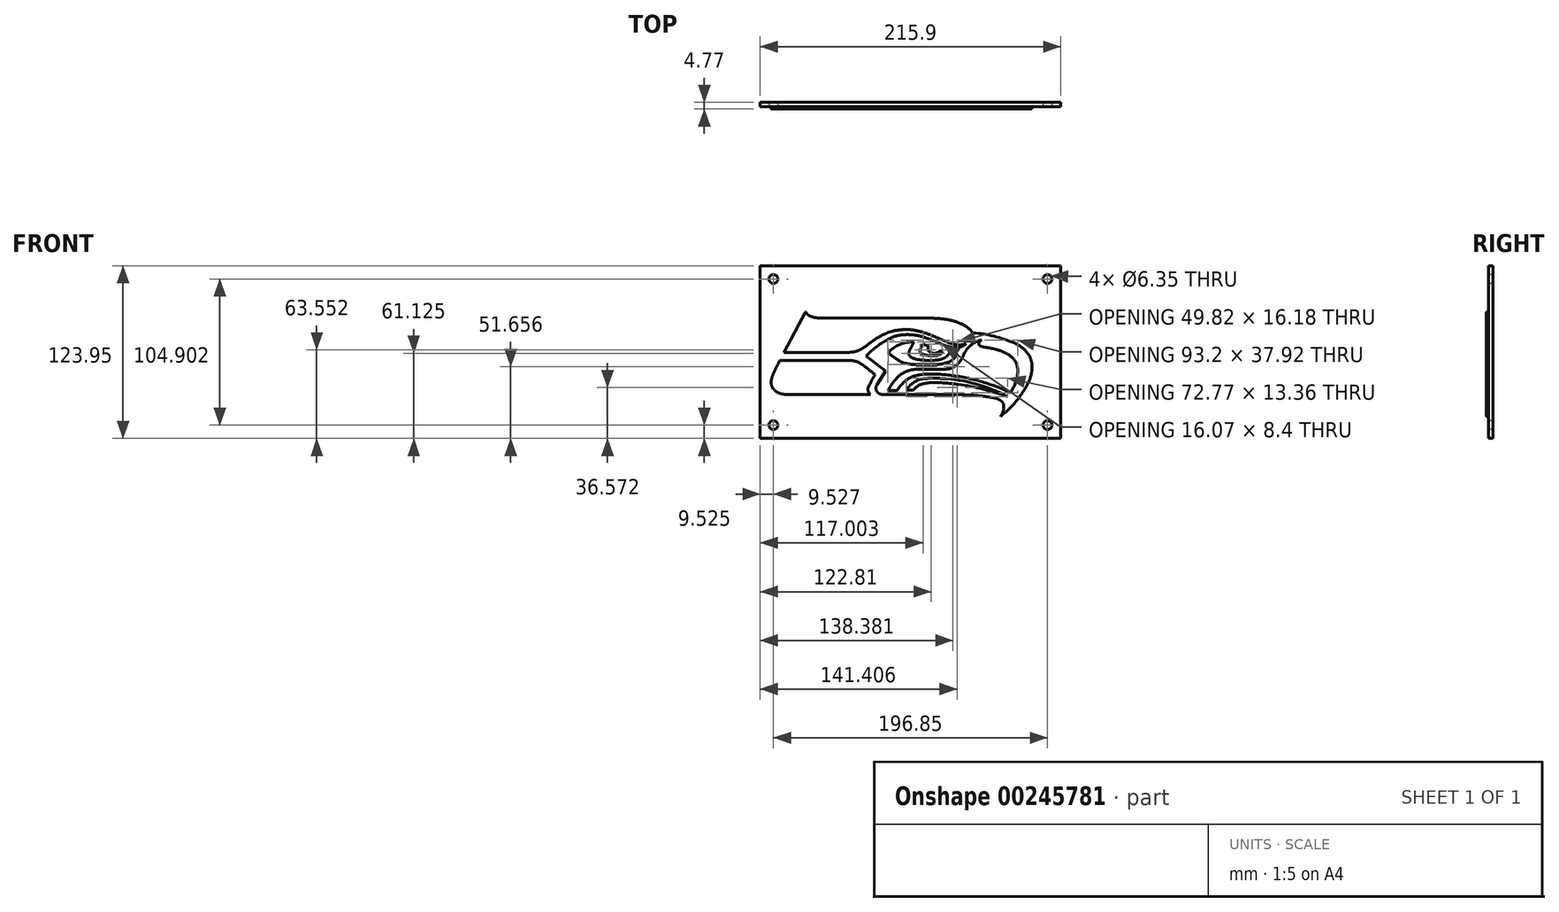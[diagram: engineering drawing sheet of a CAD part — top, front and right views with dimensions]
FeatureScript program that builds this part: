
annotation { "Feature Type Name" : "Feature", "Feature Type Description" : "" }
export const myFeature = defineFeature(function(context is Context, id is Id, definition is map)
    precondition{}
    {
        {
            var Q0;
            Q0=qCreatedBy(makeId("Front.planeOp"),FACE);
            var sketch = newSketch(context, id + "F0", { "sketchPlane" : qUnion([Q0])});
            skPoint(sketch, "E0", {"position": v(83.1, -14.56) * mm});
            skPoint(sketch, "E1", {"position": v(53.3, 23.61) * mm});
            skPoint(sketch, "E2", {"position": v(-2.59, 17.22) * mm});
            skPoint(sketch, "E3", {"position": v(-18.44, 14.8) * mm});
            skLineSegment(sketch, "E4", {"start": v(-77.5, 17.11) * mm, "end": v(-61.9, 46.38) * mm});
            skPoint(sketch, "E5", {"position": v(-77.5, 17.11) * mm});
            skLineSegment(sketch, "E6", {"start": v(-80.45, 11.57) * mm, "end": v(-32.35, 11.57) * mm});
            skLineSegment(sketch, "E7", {"start": v(-77.5, 17.11) * mm, "end": v(-36.51, 17.11) * mm});
            skPoint(sketch, "E8", {"position": v(-4.71, 3.77) * mm});
            skPoint(sketch, "E9", {"position": v(-12.17, 1.23) * mm});
            skLineSegment(sketch, "E10", {"start": v(-18.44, 14.8) * mm, "end": v(-4.71, 3.77) * mm});
            skPoint(sketch, "E11", {"position": v(48.88, -13.09) * mm});
            skPoint(sketch, "E12", {"position": v(3.66, -13.09) * mm});
            skLineSegment(sketch, "E13", {"start": v(3.66, -13.09) * mm, "end": v(48.88, -13.09) * mm});
            skPoint(sketch, "E14", {"position": v(27.95, 41.83) * mm});
            skPoint(sketch, "E15", {"position": v(-50.49, 41.83) * mm});
            skLineSegment(sketch, "E16", {"start": v(-50.49, 41.83) * mm, "end": v(27.95, 41.83) * mm});
            skPoint(sketch, "E17", {"position": v(-15.51, -13.08) * mm});
            skPoint(sketch, "E18", {"position": v(-72.6, -13.08) * mm});
            skLineSegment(sketch, "E19", {"start": v(-72.6, -13.08) * mm, "end": v(-15.51, -13.08) * mm});
            skArc(sketch, "E20", {"start": v(-80.45, 11.57) * mm, "mid": v(-82.64, 7.5) * mm, "end": v(-84.65, 3.32) * mm});
            skArc(sketch, "E21", {"start": v(-84.65, 3.32) * mm, "mid": v(-85.98, 0.1) * mm, "end": v(-86.75, -3.29) * mm});
            skArc(sketch, "E22", {"start": v(-86.75, -3.29) * mm, "mid": v(-86.53, -6.36) * mm, "end": v(-85.07, -9.07) * mm});
            skArc(sketch, "E23", {"start": v(-85.07, -9.07) * mm, "mid": v(-83.8, -10.4) * mm, "end": v(-82.26, -11.42) * mm});
            skArc(sketch, "E24", {"start": v(-82.26, -11.42) * mm, "mid": v(-79.46, -12.44) * mm, "end": v(-76.5, -12.87) * mm});
            skArc(sketch, "E25", {"start": v(-76.5, -12.87) * mm, "mid": v(-74.55, -13.03) * mm, "end": v(-72.6, -13.08) * mm});
            skArc(sketch, "E26", {"start": v(-17.23, -9.28) * mm, "mid": v(-16.72, -11.33) * mm, "end": v(-15.51, -13.08) * mm});
            skArc(sketch, "E27", {"start": v(-16.87, -7.42) * mm, "mid": v(-17.14, -8.33) * mm, "end": v(-17.23, -9.28) * mm});
            skArc(sketch, "E28", {"start": v(-12.17, 1.23) * mm, "mid": v(-14.63, -3.04) * mm, "end": v(-16.87, -7.42) * mm});
            skArc(sketch, "E29", {"start": v(-12.17, 1.23) * mm, "mid": v(-15.75, 4.2) * mm, "end": v(-19.4, 7.08) * mm});
            skArc(sketch, "E30", {"start": v(-19.4, 7.08) * mm, "mid": v(-21.67, 8.77) * mm, "end": v(-24.1, 10.24) * mm});
            skArc(sketch, "E31", {"start": v(-24.1, 10.24) * mm, "mid": v(-25.94, 10.88) * mm, "end": v(-27.86, 11.3) * mm});
            skArc(sketch, "E32", {"start": v(-27.86, 11.3) * mm, "mid": v(-30.1, 11.5) * mm, "end": v(-32.35, 11.57) * mm});
            skArc(sketch, "E33", {"start": v(-61.9, 46.38) * mm, "mid": v(-61.6, 45.72) * mm, "end": v(-61.17, 45.13) * mm});
            skArc(sketch, "E34", {"start": v(-61.17, 45.13) * mm, "mid": v(-60.08, 44.13) * mm, "end": v(-58.82, 43.35) * mm});
            skArc(sketch, "E35", {"start": v(-58.82, 43.35) * mm, "mid": v(-54.73, 42.22) * mm, "end": v(-50.49, 41.83) * mm});
            skPoint(sketch, "E36", {"position": v(15.73, 24.77) * mm});
            skPoint(sketch, "E37", {"position": v(22.28, 23.3) * mm});
            skArc(sketch, "E38", {"start": v(-36.51, 17.11) * mm, "mid": v(-32.76, 17.2) * mm, "end": v(-29.02, 17.45) * mm});
            skArc(sketch, "E39", {"start": v(-29.02, 17.45) * mm, "mid": v(-25.84, 18) * mm, "end": v(-22.84, 19.23) * mm});
            skArc(sketch, "E40", {"start": v(-22.84, 19.23) * mm, "mid": v(-19.58, 21.2) * mm, "end": v(-16.56, 23.52) * mm});
            skArc(sketch, "E41", {"start": v(-4.04, 31.03) * mm, "mid": v(-10.55, 27.69) * mm, "end": v(-16.56, 23.52) * mm});
            skArc(sketch, "E42", {"start": v(5.12, 33.37) * mm, "mid": v(0.45, 32.54) * mm, "end": v(-4.04, 31.03) * mm});
            skArc(sketch, "E43", {"start": v(17.75, 32.87) * mm, "mid": v(11.46, 33.66) * mm, "end": v(5.12, 33.37) * mm});
            skArc(sketch, "E44", {"start": v(29.14, 29.25) * mm, "mid": v(23.53, 31.33) * mm, "end": v(17.75, 32.87) * mm});
            skArc(sketch, "E45", {"start": v(29.14, 29.25) * mm, "mid": v(33.48, 27.38) * mm, "end": v(37.82, 25.5) * mm});
            skArc(sketch, "E46", {"start": v(37.82, 25.5) * mm, "mid": v(41.16, 24.17) * mm, "end": v(44.62, 23.16) * mm});
            skArc(sketch, "E47", {"start": v(44.62, 23.16) * mm, "mid": v(47.08, 22.77) * mm, "end": v(49.56, 22.76) * mm});
            skArc(sketch, "E48", {"start": v(49.56, 22.76) * mm, "mid": v(51.46, 23.05) * mm, "end": v(53.3, 23.61) * mm});
            skPoint(sketch, "E49", {"position": v(58.16, 31.3) * mm});
            skArc(sketch, "E50", {"start": v(46.67, 20.92) * mm, "mid": v(50.24, 21.64) * mm, "end": v(53.3, 23.61) * mm});
            skArc(sketch, "E51", {"start": v(42.4, 21.15) * mm, "mid": v(44.53, 20.93) * mm, "end": v(46.67, 20.92) * mm});
            skArc(sketch, "E52", {"start": v(36.65, 22.8) * mm, "mid": v(39.47, 21.8) * mm, "end": v(42.4, 21.15) * mm});
            skArc(sketch, "E53", {"start": v(36.65, 22.8) * mm, "mid": v(31.5, 24.87) * mm, "end": v(26.36, 26.94) * mm});
            skArc(sketch, "E54", {"start": v(26.36, 26.94) * mm, "mid": v(22.83, 28.25) * mm, "end": v(19.2, 29.25) * mm});
            skArc(sketch, "E55", {"start": v(19.2, 29.25) * mm, "mid": v(13.6, 30) * mm, "end": v(7.95, 29.93) * mm});
            skArc(sketch, "E56", {"start": v(7.95, 29.93) * mm, "mid": v(2.8, 29) * mm, "end": v(-2.05, 27.06) * mm});
            skArc(sketch, "E57", {"start": v(-2.05, 27.06) * mm, "mid": v(-10.74, 21.59) * mm, "end": v(-18.44, 14.8) * mm});
            skPoint(sketch, "E58", {"position": v(-4.1, -13.09) * mm});
            skLineSegment(sketch, "E59", {"start": v(-4.1, -13.09) * mm, "end": v(3.66, -13.09) * mm});
            skLineSegment(sketch, "E60", {"start": v(-4.1, -13.09) * mm, "end": v(-5.96, -13.09) * mm});
            skArc(sketch, "E61", {"start": v(-9.44, -12.15) * mm, "mid": v(-7.76, -12.85) * mm, "end": v(-5.96, -13.09) * mm});
            skArc(sketch, "E62", {"start": v(-11.4, -9.51) * mm, "mid": v(-10.66, -11) * mm, "end": v(-9.44, -12.15) * mm});
            skArc(sketch, "E63", {"start": v(-10.74, -5.6) * mm, "mid": v(-11.44, -7.5) * mm, "end": v(-11.4, -9.51) * mm});
            skLineSegment(sketch, "E64", {"start": v(-4.71, 3.77) * mm, "end": v(-10.74, -5.6) * mm});
            skPoint(sketch, "E65", {"position": v(77.83, -28.7) * mm});
            skArc(sketch, "E66", {"start": v(41.18, 40.57) * mm, "mid": v(34.6, 41.52) * mm, "end": v(27.95, 41.83) * mm});
            skArc(sketch, "E67", {"start": v(50.53, 37.46) * mm, "mid": v(45.95, 39.31) * mm, "end": v(41.18, 40.57) * mm});
            skArc(sketch, "E68", {"start": v(58.16, 31.3) * mm, "mid": v(54.66, 34.77) * mm, "end": v(50.53, 37.46) * mm});
            skArc(sketch, "E69", {"start": v(87.67, 24.07) * mm, "mid": v(73.22, 28.92) * mm, "end": v(58.16, 31.3) * mm});
            skArc(sketch, "E70", {"start": v(96.52, 17.84) * mm, "mid": v(92.46, 21.47) * mm, "end": v(87.67, 24.07) * mm});
            skArc(sketch, "E71", {"start": v(100.12, 11.11) * mm, "mid": v(98.73, 14.7) * mm, "end": v(96.52, 17.84) * mm});
            skArc(sketch, "E72", {"start": v(100.61, 6.88) * mm, "mid": v(100.5, 9) * mm, "end": v(100.12, 11.11) * mm});
            skArc(sketch, "E73", {"start": v(100.12, 1.89) * mm, "mid": v(100.5, 4.37) * mm, "end": v(100.61, 6.88) * mm});
            skArc(sketch, "E74", {"start": v(96.6, -6.91) * mm, "mid": v(98.68, -2.64) * mm, "end": v(100.12, 1.89) * mm});
            skArc(sketch, "E75", {"start": v(92.65, -13.2) * mm, "mid": v(94.72, -10.1) * mm, "end": v(96.6, -6.91) * mm});
            skArc(sketch, "E76", {"start": v(77.83, -28.7) * mm, "mid": v(85.84, -21.52) * mm, "end": v(92.65, -13.2) * mm});
            skArc(sketch, "E77", {"start": v(66.8, -14.37) * mm, "mid": v(57.86, -13.4) * mm, "end": v(48.88, -13.09) * mm});
            skArc(sketch, "E78", {"start": v(72, -15.16) * mm, "mid": v(69.4, -14.7) * mm, "end": v(66.8, -14.37) * mm});
            skArc(sketch, "E79", {"start": v(76.2, -16.26) * mm, "mid": v(74.13, -15.57) * mm, "end": v(72, -15.16) * mm});
            skArc(sketch, "E80", {"start": v(80.12, -20.01) * mm, "mid": v(78.54, -17.74) * mm, "end": v(76.2, -16.26) * mm});
            skArc(sketch, "E81", {"start": v(77.83, -28.7) * mm, "mid": v(80, -24.62) * mm, "end": v(80.12, -20.01) * mm});
            skArc(sketch, "E82", {"start": v(15.73, 24.77) * mm, "mid": v(5.76, 22.96) * mm, "end": v(-2.59, 17.22) * mm});
            skLineSegment(sketch, "E83", {"start": v(15.73, 24.77) * mm, "end": v(13.68, 20.97) * mm});
            skArc(sketch, "E84", {"start": v(-2.59, 17.22) * mm, "mid": v(0.74, 14.29) * mm, "end": v(4.36, 11.73) * mm});
            skArc(sketch, "E85", {"start": v(4.36, 11.73) * mm, "mid": v(8.03, 9.89) * mm, "end": v(12.04, 8.96) * mm});
            skLineSegment(sketch, "E86", {"start": v(17.17, 8.58) * mm, "end": v(31.1, 8.58) * mm});
            skArc(sketch, "E87", {"start": v(12.04, 8.96) * mm, "mid": v(14.6, 8.68) * mm, "end": v(17.17, 8.58) * mm});
            skPoint(sketch, "E88", {"position": v(47.23, 16.72) * mm});
            skPoint(sketch, "E89", {"position": v(41.25, 16.75) * mm});
            skArc(sketch, "E90", {"start": v(41.25, 16.75) * mm, "mid": v(44.24, 16.5) * mm, "end": v(47.23, 16.72) * mm});
            skArc(sketch, "E91", {"start": v(31.1, 8.58) * mm, "mid": v(35.69, 8.98) * mm, "end": v(40.14, 10.15) * mm});
            skArc(sketch, "E92", {"start": v(40.14, 10.15) * mm, "mid": v(44.37, 12.7) * mm, "end": v(47.23, 16.72) * mm});
            skArc(sketch, "E93", {"start": v(37.97, 13.54) * mm, "mid": v(39.82, 14.94) * mm, "end": v(41.25, 16.75) * mm});
            skArc(sketch, "E94", {"start": v(34.3, 12.11) * mm, "mid": v(36.2, 12.68) * mm, "end": v(37.97, 13.54) * mm});
            skArc(sketch, "E95", {"start": v(30.78, 11.64) * mm, "mid": v(32.55, 11.82) * mm, "end": v(34.3, 12.11) * mm});
            skArc(sketch, "E96", {"start": v(23.67, 11.64) * mm, "mid": v(27.23, 11.54) * mm, "end": v(30.78, 11.64) * mm});
            skArc(sketch, "E97", {"start": v(14.87, 13.15) * mm, "mid": v(19.21, 12.06) * mm, "end": v(23.67, 11.64) * mm});
            skArc(sketch, "E98", {"start": v(12.29, 15.66) * mm, "mid": v(13.34, 14.16) * mm, "end": v(14.87, 13.15) * mm});
            skArc(sketch, "E99", {"start": v(12.36, 17.99) * mm, "mid": v(12.07, 16.83) * mm, "end": v(12.29, 15.66) * mm});
            skArc(sketch, "E100", {"start": v(13.68, 20.97) * mm, "mid": v(12.96, 19.5) * mm, "end": v(12.36, 17.99) * mm});
            skLineSegment(sketch, "E101", {"start": v(22.28, 23.3) * mm, "end": v(26.52, 21.7) * mm});
            skArc(sketch, "E102", {"start": v(22.28, 23.3) * mm, "mid": v(21.3, 21.75) * mm, "end": v(20.45, 20.12) * mm});
            skArc(sketch, "E103", {"start": v(20.45, 20.12) * mm, "mid": v(20.15, 19.16) * mm, "end": v(20.1, 18.16) * mm});
            skArc(sketch, "E104", {"start": v(20.1, 18.16) * mm, "mid": v(20.54, 17.1) * mm, "end": v(21.42, 16.35) * mm});
            skLineSegment(sketch, "E105", {"start": v(28.8, 14.9) * mm, "end": v(30.76, 14.9) * mm});
            skPoint(sketch, "E106", {"position": v(26.35, 15.05) * mm});
            skPoint(sketch, "E107", {"position": v(21.42, 16.35) * mm});
            skArc(sketch, "E108", {"start": v(21.42, 16.35) * mm, "mid": v(23.82, 15.45) * mm, "end": v(26.35, 15.05) * mm});
            skArc(sketch, "E109", {"start": v(26.35, 15.05) * mm, "mid": v(27.57, 14.94) * mm, "end": v(28.8, 14.9) * mm});
            skPoint(sketch, "E110", {"position": v(36.17, 17.74) * mm});
            skArc(sketch, "E111", {"start": v(30.76, 14.9) * mm, "mid": v(31.83, 14.95) * mm, "end": v(32.9, 15.08) * mm});
            skArc(sketch, "E112", {"start": v(32.9, 15.08) * mm, "mid": v(34.83, 16.04) * mm, "end": v(36.17, 17.74) * mm});
            skPoint(sketch, "E113", {"position": v(34.56, 18.42) * mm});
            skLineSegment(sketch, "E114", {"start": v(36.17, 17.74) * mm, "end": v(34.56, 18.42) * mm});
            skArc(sketch, "E115", {"start": v(26.52, 21.7) * mm, "mid": v(26, 20.99) * mm, "end": v(25.76, 20.13) * mm});
            skArc(sketch, "E116", {"start": v(25.76, 20.13) * mm, "mid": v(25.84, 19.24) * mm, "end": v(26.24, 18.43) * mm});
            skPoint(sketch, "E117", {"position": v(27.28, 17.44) * mm});
            skArc(sketch, "E118", {"start": v(26.24, 18.43) * mm, "mid": v(26.7, 17.88) * mm, "end": v(27.28, 17.44) * mm});
            skPoint(sketch, "E119", {"position": v(31.08, 16.73) * mm});
            skArc(sketch, "E120", {"start": v(27.28, 17.44) * mm, "mid": v(29.13, 16.8) * mm, "end": v(31.08, 16.73) * mm});
            skArc(sketch, "E121", {"start": v(31.08, 16.73) * mm, "mid": v(32.95, 17.3) * mm, "end": v(34.56, 18.42) * mm});
            skLineSegment(sketch, "E122", {"start": v(-2.77, -10.1) * mm, "end": v(3.72, -10.1) * mm});
            skLineSegment(sketch, "E123", {"start": v(-2.77, -10.1) * mm, "end": v(-2.9, -10.1) * mm});
            skPoint(sketch, "E124", {"position": v(0.3, -5.03) * mm});
            skArc(sketch, "E125", {"start": v(0.3, -5.03) * mm, "mid": v(-1.36, -7.52) * mm, "end": v(-2.9, -10.1) * mm});
            skArc(sketch, "E126", {"start": v(5.39, 0.57) * mm, "mid": v(2.65, -2.06) * mm, "end": v(0.3, -5.03) * mm});
            skArc(sketch, "E127", {"start": v(12.79, 4.41) * mm, "mid": v(8.86, 2.93) * mm, "end": v(5.39, 0.57) * mm});
            skArc(sketch, "E128", {"start": v(18.73, 5.24) * mm, "mid": v(15.73, 5.01) * mm, "end": v(12.79, 4.41) * mm});
            skLineSegment(sketch, "E129", {"start": v(18.73, 5.24) * mm, "end": v(37.98, 5.24) * mm});
            skArc(sketch, "E130", {"start": v(37.98, 5.24) * mm, "mid": v(40.65, 5.47) * mm, "end": v(43.24, 6.17) * mm});
            skArc(sketch, "E131", {"start": v(43.24, 6.17) * mm, "mid": v(45.94, 7.84) * mm, "end": v(48.26, 10) * mm});
            skArc(sketch, "E132", {"start": v(48.26, 10) * mm, "mid": v(49.92, 12.5) * mm, "end": v(51.34, 15.16) * mm});
            skArc(sketch, "E133", {"start": v(60.64, 25) * mm, "mid": v(55.05, 20.97) * mm, "end": v(51.34, 15.16) * mm});
            skPoint(sketch, "E134", {"position": v(64.26, 26.17) * mm});
            skArc(sketch, "E135", {"start": v(64.26, 26.17) * mm, "mid": v(62.4, 25.71) * mm, "end": v(60.64, 25) * mm});
            skArc(sketch, "E136", {"start": v(64.26, 26.17) * mm, "mid": v(63.54, 25.6) * mm, "end": v(62.93, 24.92) * mm});
            skPoint(sketch, "E137", {"position": v(65.71, 21.3) * mm});
            skPoint(sketch, "E138", {"position": v(65.71, 21.23) * mm});
            skArc(sketch, "E139", {"start": v(62.93, 24.92) * mm, "mid": v(62.7, 24.55) * mm, "end": v(62.49, 24.16) * mm});
            skPoint(sketch, "E140", {"position": v(65.7, 21.16) * mm});
            skArc(sketch, "E141", {"start": v(62.49, 24.16) * mm, "mid": v(62.33, 23.71) * mm, "end": v(62.3, 23.24) * mm});
            skArc(sketch, "E142", {"start": v(62.3, 23.24) * mm, "mid": v(62.45, 22.68) * mm, "end": v(62.87, 22.27) * mm});
            skArc(sketch, "E143", {"start": v(62.87, 22.27) * mm, "mid": v(64.23, 21.58) * mm, "end": v(65.7, 21.16) * mm});
            skArc(sketch, "E144", {"start": v(73.3, 19.8) * mm, "mid": v(69.52, 20.57) * mm, "end": v(65.7, 21.16) * mm});
            skArc(sketch, "E145", {"start": v(80.92, 17.2) * mm, "mid": v(77.17, 18.69) * mm, "end": v(73.3, 19.8) * mm});
            skArc(sketch, "E146", {"start": v(87.1, 12.73) * mm, "mid": v(84.27, 15.32) * mm, "end": v(80.92, 17.2) * mm});
            skArc(sketch, "E147", {"start": v(90.25, 5.38) * mm, "mid": v(89.29, 9.32) * mm, "end": v(87.1, 12.73) * mm});
            skArc(sketch, "E148", {"start": v(89.94, -0.1) * mm, "mid": v(90.27, 2.63) * mm, "end": v(90.25, 5.38) * mm});
            skArc(sketch, "E149", {"start": v(85.04, -11.76) * mm, "mid": v(88, -6.15) * mm, "end": v(89.94, -0.1) * mm});
            skArc(sketch, "E150", {"start": v(85.04, -11.76) * mm, "mid": v(78.9, -8.92) * mm, "end": v(72.62, -6.41) * mm});
            skPoint(sketch, "E151", {"position": v(46.62, 0.2) * mm});
            skArc(sketch, "E152", {"start": v(72.62, -6.41) * mm, "mid": v(59.77, -2.5) * mm, "end": v(46.62, 0.2) * mm});
            skArc(sketch, "E153", {"start": v(46.62, 0.2) * mm, "mid": v(36.07, 1.4) * mm, "end": v(25.45, 1.7) * mm});
            skArc(sketch, "E154", {"start": v(25.45, 1.7) * mm, "mid": v(21.35, 1.39) * mm, "end": v(17.3, 0.64) * mm});
            skArc(sketch, "E155", {"start": v(17.3, 0.64) * mm, "mid": v(11.85, -1.61) * mm, "end": v(7.33, -5.4) * mm});
            skArc(sketch, "E156", {"start": v(7.33, -5.4) * mm, "mid": v(5.37, -7.63) * mm, "end": v(3.72, -10.1) * mm});
            skArc(sketch, "E157", {"start": v(35.8, -1.44) * mm, "mid": v(29.24, -1.2) * mm, "end": v(22.69, -1.62) * mm});
            skArc(sketch, "E158", {"start": v(22.69, -1.62) * mm, "mid": v(15.53, -4.32) * mm, "end": v(10.34, -9.93) * mm});
            skLineSegment(sketch, "E159", {"start": v(10.34, -9.93) * mm, "end": v(15.46, -9.93) * mm});
            skArc(sketch, "E160", {"start": v(22.36, -5.23) * mm, "mid": v(18.46, -6.92) * mm, "end": v(15.46, -9.93) * mm});
            skArc(sketch, "E161", {"start": v(83.1, -14.56) * mm, "mid": v(65.67, -9.1) * mm, "end": v(47.7, -5.74) * mm});
            skArc(sketch, "E162", {"start": v(47.7, -5.74) * mm, "mid": v(38.8, -4.7) * mm, "end": v(29.86, -4.3) * mm});
            skArc(sketch, "E163", {"start": v(29.86, -4.3) * mm, "mid": v(26.1, -4.6) * mm, "end": v(22.36, -5.23) * mm});
            skArc(sketch, "E164", {"start": v(83.1, -14.56) * mm, "mid": v(60.19, -5.37) * mm, "end": v(35.8, -1.44) * mm});
            skLineSegment(sketch, "E165", {"start": v(26.52, 21.7) * mm, "end": v(34.56, 18.42) * mm});
            skSolve(sketch);
        }
        {
            var Q0;
            Q0=makeQuery(id+"F0.imprint","IMPRINT",FACE,{"disambiguationData":[TD([[makeQuery(id+"F0.imprint","IMPRINT",EDGE,{"derivedFrom":sQuery(id+"F0.wireOp",EDGE,"E4")}),-1.0]])]});
            var Q1;
            Q1=makeQuery(id+"F0.imprint","IMPRINT",FACE,{"disambiguationData":[TD([[makeQuery(id+"F0.imprint","IMPRINT",EDGE,{"derivedFrom":sQuery(id+"F0.wireOp",EDGE,"E6")}),-1.0]])]});
            var Q2;
            Q2=makeQuery(id+"F0.imprint","IMPRINT",FACE,{"disambiguationData":[TD([[makeQuery(id+"F0.imprint","IMPRINT",EDGE,{"derivedFrom":sQuery(id+"F0.wireOp",EDGE,"E115")}),1.0]])]});
            extrude(context, id + "F1", {"entities" : qUnion([Q0, Q1, Q2]), "depth" : 1.59 * mm});
        }
        {
            var Q0;
            Q0=qCreatedBy(makeId("Front.planeOp"),FACE);
            var sketch = newSketch(context, id + "F2", { "sketchPlane" : qUnion([Q0])});
            skLineSegment(sketch, "E166.bottom", {"start": v(-94.68, 79.5) * mm, "end": v(121.22, 79.5) * mm});
            skLineSegment(sketch, "E166.top", {"start": v(-94.68, -44.45) * mm, "end": v(121.22, -44.45) * mm});
            skLineSegment(sketch, "E166.left", {"start": v(-94.68, 79.5) * mm, "end": v(-94.68, -44.45) * mm});
            skLineSegment(sketch, "E166.right", {"start": v(121.22, 79.5) * mm, "end": v(121.22, -44.45) * mm});
            skSolve(sketch);
        }
        {
            var Q0;
            Q0=makeQuery(id+"F2.imprint","IMPRINT",FACE,{"disambiguationData":[TD([[makeQuery(id+"F2.imprint","IMPRINT",EDGE,{"derivedFrom":sQuery(id+"F2.wireOp",EDGE,"E166.bottom")}),-1.0]])]});
            extrude(context, id + "F5", {"entities" : qUnion([Q0]), "oppositeDirection" : true, "depth" : 3.17 * mm});
        }
        {
            var Q0;
            Q0=qCreatedBy(makeId("Front.planeOp"),FACE);
            var sketch = newSketch(context, id + "F3", { "sketchPlane" : qUnion([Q0])});
            skPoint(sketch, "E167", {"position": v(-85.15, 69.98) * mm});
            skPoint(sketch, "E168", {"position": v(111.7, 69.98) * mm});
            skPoint(sketch, "E169", {"position": v(111.7, -34.93) * mm});
            skPoint(sketch, "E170", {"position": v(-85.15, -34.93) * mm});
            skSolve(sketch);
        }
        {
            var Q0;
            Q0=sQuery(id+"F3.wireOp",VERTEX,"E167");
            var Q1;
            Q1=sQuery(id+"F3.wireOp",VERTEX,"E168");
            var Q2;
            Q2=sQuery(id+"F3.wireOp",VERTEX,"E170");
            var Q3;
            Q3=sQuery(id+"F3.wireOp",VERTEX,"E169");
            var Q4;
            Q4=makeQuery(id+"F5.opExtrude","SWEPT_BODY",BODY,{"disambiguationData":[OSD([sQuery(id+"F2.wireOp",EDGE,"E166.bottom"),sQuery(id+"F2.wireOp",EDGE,"E166.top"),sQuery(id+"F2.wireOp",EDGE,"E166.left"),sQuery(id+"F2.wireOp",EDGE,"E166.right")])]});
            hole(context, id + "F4", {"style" : HoleStyle.SIMPLE, "endStyle" : HoleEndStyle.THROUGH, "holeDiameter" : 6.35 * mm, "tappedDepth" : 12.7 * mm, "tapClearance" : 3, "locations" : qUnion([Q0, Q1, Q2, Q3]), "scope" : qUnion([Q4])});
        }
    });
